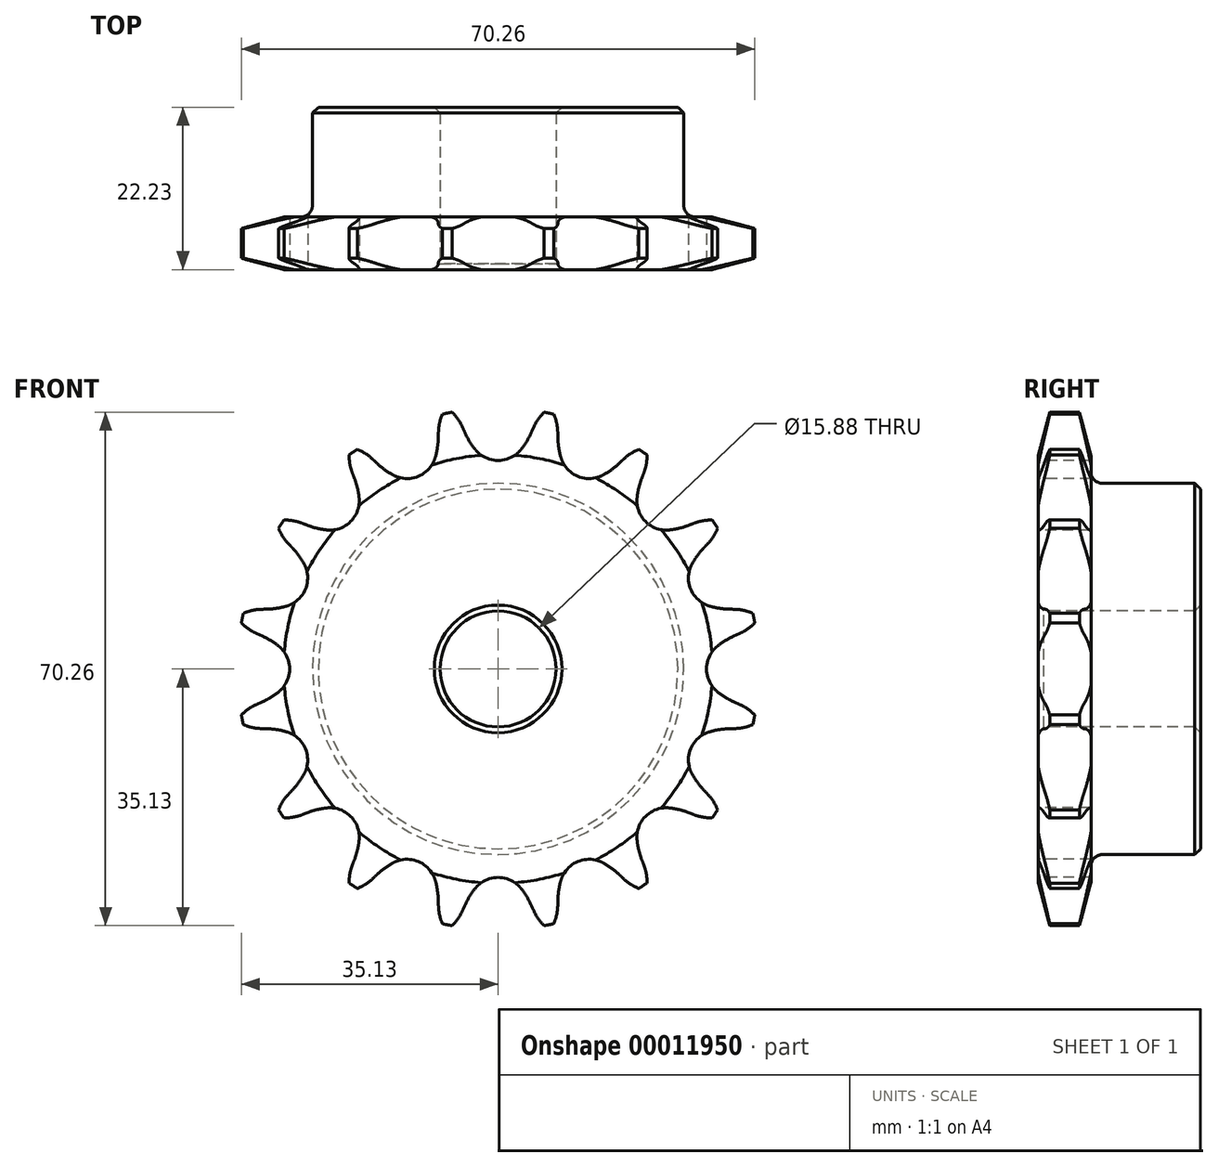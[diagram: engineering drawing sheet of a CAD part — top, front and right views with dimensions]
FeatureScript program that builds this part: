
annotation { "Feature Type Name" : "Feature", "Feature Type Description" : "" }
export const myFeature = defineFeature(function(context is Context, id is Id, definition is map)
    precondition{}
    {
        {
            var Q0;
            Q0=qCreatedBy(makeId("Right.planeOp"),FACE);
            var sketch = newSketch(context, id + "F0", { "sketchPlane" : qUnion([Q0])});
            skLineSegment(sketch, "E0", {"start": v(0, 0) * mm, "end": v(22.22, 0) * mm, "construction": true});
            skLineSegment(sketch, "E1", {"start": v(0, 35.69) * mm, "end": v(7.21, 35.69) * mm});
            skLineSegment(sketch, "E2", {"start": v(7.21, 35.69) * mm, "end": v(7.21, 25.4) * mm});
            skLineSegment(sketch, "E3", {"start": v(7.21, 25.4) * mm, "end": v(22.23, 25.4) * mm});
            skLineSegment(sketch, "E4", {"start": v(22.22, 25.4) * mm, "end": v(22.22, 7.94) * mm});
            skLineSegment(sketch, "E5", {"start": v(22.23, 7.94) * mm, "end": v(0, 7.94) * mm});
            skLineSegment(sketch, "E6", {"start": v(0, 7.94) * mm, "end": v(0, 35.69) * mm});
            skLineSegment(sketch, "E7.0.MirrorCS", {"start": v(0, -35.69) * mm, "end": v(7.21, -35.69) * mm});
            skLineSegment(sketch, "E7.1.MirrorCS", {"start": v(7.21, -35.69) * mm, "end": v(7.21, -25.4) * mm});
            skLineSegment(sketch, "E7.2.MirrorCS", {"start": v(22.23, -7.94) * mm, "end": v(0, -7.94) * mm});
            skLineSegment(sketch, "E7.3.MirrorCS", {"start": v(22.23, -25.4) * mm, "end": v(22.23, -7.94) * mm});
            skLineSegment(sketch, "E7.4.MirrorCS", {"start": v(7.21, -25.4) * mm, "end": v(22.23, -25.4) * mm});
            skLineSegment(sketch, "E7.5.MirrorCS", {"start": v(0, -7.94) * mm, "end": v(0, -35.69) * mm});
            skSolve(sketch);
        }
        {
            var Q0;
            Q0=makeQuery(id+"F0.imprint","IMPRINT",FACE,{"disambiguationData":[TD([[makeQuery(id+"F0.imprint","IMPRINT",EDGE,{"derivedFrom":sQuery(id+"F0.wireOp",EDGE,"E1")}),-1.0]])]});
            var Q1;
            Q1=sQuery(id+"F0.wireOp",EDGE,"E0");
            revolve(context, id + "F1", {"entities" : qUnion([Q0]), "axis" : qUnion([Q1]), "revolveType" : RevolveType.FULL});
        }
        {
            var Q0;
            Q0=makeQuery(id+"F1.opRevolve","SWEPT_EDGE",EDGE,{"disambiguationData":[OSD([sQuery(id+"F0.wireOp",EDGE,"E1"),sQuery(id+"F0.wireOp",EDGE,"E6")])]});
            var Q1;
            Q1=makeQuery(id+"F1.opRevolve","SWEPT_EDGE",EDGE,{"disambiguationData":[OSD([sQuery(id+"F0.wireOp",EDGE,"E1"),sQuery(id+"F0.wireOp",EDGE,"E2")])]});
            chamfer(context, id + "F2", {"entities" : qUnion([Q0, Q1]), "chamferType" : ChamferType.TWO_OFFSETS, "width1" : 6.35 * mm, "oppositeDirection" : false, "width2" : 1.57 * mm, "tangentPropagation" : true});
        }
        {
            var Q0;
            Q0=makeQuery(id+"F1.opRevolve","SWEPT_FACE",FACE,{"disambiguationData":[OSD([sQuery(id+"F0.wireOp",EDGE,"E6")])]});
            var sketch = newSketch(context, id + "F3", { "sketchPlane" : qUnion([Q0])});
            skCircle(sketch, "E8", {"center": v(0, 0) * mm, "radius": 32.55 * mm, "construction": true});
            skLineSegment(sketch, "E9", {"start": v(0, 0) * mm, "end": v(0, 32.55) * mm, "construction": true});
            skLineSegment(sketch, "E10", {"start": v(0, 32.55) * mm, "end": v(25.8, 32.55) * mm, "construction": true});
            skPoint(sketch, "E11", {"position": v(-10.88, 30.38) * mm});
            skPoint(sketch, "E12", {"position": v(4.95, 36.52) * mm});
            skLineSegment(sketch, "E13", {"start": v(0, 32.55) * mm, "end": v(4.95, 36.52) * mm, "construction": true});
            skLineSegment(sketch, "E14", {"start": v(4.95, 36.52) * mm, "end": v(-4.5, 32.26) * mm, "construction": true});
            skLineSegment(sketch, "E15", {"start": v(-4.5, 32.26) * mm, "end": v(-4.88, 33.1) * mm});
            skLineSegment(sketch, "E16", {"start": v(0, 0) * mm, "end": v(-7.12, 35.8) * mm, "construction": true});
            skArc(sketch, "E17", {"start": v(-7.12, 35.8) * mm, "mid": v(-15.95, 26.17) * mm, "end": v(-4.88, 33.1) * mm, "construction": true});
            skArc(sketch, "E18", {"start": v(-4.88, 33.1) * mm, "mid": v(-5.81, 34.6) * mm, "end": v(-7.12, 35.8) * mm});
            skArc(sketch, "E19", {"start": v(-3.14, 30.03) * mm, "mid": v(13.78, 41.93) * mm, "end": v(-4.5, 32.26) * mm, "construction": true});
            skArc(sketch, "E20", {"start": v(-4.5, 32.26) * mm, "mid": v(-3.89, 31.1) * mm, "end": v(-3.14, 30.03) * mm});
            skLineSegment(sketch, "E21", {"start": v(4.4, 12.5) * mm, "end": v(-4.88, 33.1) * mm, "construction": true});
            skArc(sketch, "E22.0.MirrorCS", {"start": v(4.5, 32.26) * mm, "mid": v(3.89, 31.1) * mm, "end": v(3.14, 30.03) * mm});
            skLineSegment(sketch, "E23.0.MirrorCS", {"start": v(4.5, 32.26) * mm, "end": v(4.88, 33.1) * mm});
            skArc(sketch, "E24.0.MirrorCS", {"start": v(4.88, 33.1) * mm, "mid": v(5.81, 34.6) * mm, "end": v(7.12, 35.8) * mm});
            skArc(sketch, "E25", {"start": v(-3.14, 30.03) * mm, "mid": v(0, 28.53) * mm, "end": v(3.14, 30.03) * mm});
            skArc(sketch, "E26", {"start": v(3.14, 30.03) * mm, "mid": v(0, 36.57) * mm, "end": v(-3.14, 30.03) * mm, "construction": true});
            skArc(sketch, "E27.1.0", {"start": v(-17.17, 28.7) * mm, "mid": v(-18.61, 29.74) * mm, "end": v(-20.28, 30.34) * mm});
            skLineSegment(sketch, "E27.1.1", {"start": v(-16.5, 28.08) * mm, "end": v(-17.17, 28.7) * mm});
            skArc(sketch, "E27.1.2", {"start": v(-16.5, 28.08) * mm, "mid": v(-15.5, 27.25) * mm, "end": v(-14.39, 26.55) * mm});
            skArc(sketch, "E27.1.3", {"start": v(-14.39, 26.55) * mm, "mid": v(-10.92, 26.36) * mm, "end": v(-8.6, 28.95) * mm});
            skArc(sketch, "E27.1.4", {"start": v(-8.19, 31.53) * mm, "mid": v(-8.3, 30.22) * mm, "end": v(-8.6, 28.95) * mm});
            skLineSegment(sketch, "E27.1.5", {"start": v(-8.19, 31.53) * mm, "end": v(-8.16, 32.44) * mm});
            skArc(sketch, "E27.1.6", {"start": v(-8.16, 32.44) * mm, "mid": v(-7.87, 34.19) * mm, "end": v(-7.12, 35.8) * mm});
            skArc(sketch, "E27.2.0", {"start": v(-26.85, 19.95) * mm, "mid": v(-28.57, 20.35) * mm, "end": v(-30.34, 20.28) * mm});
            skLineSegment(sketch, "E27.2.1", {"start": v(-26, 19.63) * mm, "end": v(-26.85, 19.95) * mm});
            skArc(sketch, "E27.2.2", {"start": v(-26, 19.63) * mm, "mid": v(-24.74, 19.24) * mm, "end": v(-23.45, 19.02) * mm});
            skArc(sketch, "E27.2.3", {"start": v(-23.45, 19.02) * mm, "mid": v(-20.17, 20.17) * mm, "end": v(-19.02, 23.45) * mm});
            skArc(sketch, "E27.2.4", {"start": v(-19.63, 26) * mm, "mid": v(-19.24, 24.74) * mm, "end": v(-19.02, 23.45) * mm});
            skLineSegment(sketch, "E27.2.5", {"start": v(-19.63, 26) * mm, "end": v(-19.95, 26.85) * mm});
            skArc(sketch, "E27.2.6", {"start": v(-19.95, 26.85) * mm, "mid": v(-20.35, 28.57) * mm, "end": v(-20.28, 30.34) * mm});
            skArc(sketch, "E27.3.0", {"start": v(-32.44, 8.16) * mm, "mid": v(-34.19, 7.87) * mm, "end": v(-35.8, 7.12) * mm});
            skLineSegment(sketch, "E27.3.1", {"start": v(-31.53, 8.19) * mm, "end": v(-32.44, 8.16) * mm});
            skArc(sketch, "E27.3.2", {"start": v(-31.53, 8.19) * mm, "mid": v(-30.22, 8.3) * mm, "end": v(-28.95, 8.6) * mm});
            skArc(sketch, "E27.3.3", {"start": v(-28.95, 8.6) * mm, "mid": v(-26.36, 10.92) * mm, "end": v(-26.55, 14.39) * mm});
            skArc(sketch, "E27.3.4", {"start": v(-28.08, 16.5) * mm, "mid": v(-27.25, 15.5) * mm, "end": v(-26.55, 14.39) * mm});
            skLineSegment(sketch, "E27.3.5", {"start": v(-28.08, 16.5) * mm, "end": v(-28.7, 17.17) * mm});
            skArc(sketch, "E27.3.6", {"start": v(-28.7, 17.17) * mm, "mid": v(-29.74, 18.61) * mm, "end": v(-30.34, 20.28) * mm});
            skArc(sketch, "E27.4.0", {"start": v(-33.1, -4.88) * mm, "mid": v(-34.6, -5.81) * mm, "end": v(-35.8, -7.12) * mm});
            skLineSegment(sketch, "E27.4.1", {"start": v(-32.26, -4.5) * mm, "end": v(-33.1, -4.88) * mm});
            skArc(sketch, "E27.4.2", {"start": v(-32.26, -4.5) * mm, "mid": v(-31.1, -3.89) * mm, "end": v(-30.03, -3.14) * mm});
            skArc(sketch, "E27.4.3", {"start": v(-30.03, -3.14) * mm, "mid": v(-28.53, 0) * mm, "end": v(-30.03, 3.14) * mm});
            skArc(sketch, "E27.4.4", {"start": v(-32.26, 4.5) * mm, "mid": v(-31.1, 3.89) * mm, "end": v(-30.03, 3.14) * mm});
            skLineSegment(sketch, "E27.4.5", {"start": v(-32.26, 4.5) * mm, "end": v(-33.1, 4.88) * mm});
            skArc(sketch, "E27.4.6", {"start": v(-33.1, 4.88) * mm, "mid": v(-34.6, 5.81) * mm, "end": v(-35.8, 7.12) * mm});
            skArc(sketch, "E27.5.0", {"start": v(-28.7, -17.17) * mm, "mid": v(-29.74, -18.61) * mm, "end": v(-30.34, -20.28) * mm});
            skLineSegment(sketch, "E27.5.1", {"start": v(-28.08, -16.5) * mm, "end": v(-28.7, -17.17) * mm});
            skArc(sketch, "E27.5.2", {"start": v(-28.08, -16.5) * mm, "mid": v(-27.25, -15.5) * mm, "end": v(-26.55, -14.39) * mm});
            skArc(sketch, "E27.5.3", {"start": v(-26.55, -14.39) * mm, "mid": v(-26.36, -10.92) * mm, "end": v(-28.95, -8.6) * mm});
            skArc(sketch, "E27.5.4", {"start": v(-31.53, -8.19) * mm, "mid": v(-30.22, -8.3) * mm, "end": v(-28.95, -8.6) * mm});
            skLineSegment(sketch, "E27.5.5", {"start": v(-31.53, -8.19) * mm, "end": v(-32.44, -8.16) * mm});
            skArc(sketch, "E27.5.6", {"start": v(-32.44, -8.16) * mm, "mid": v(-34.19, -7.87) * mm, "end": v(-35.8, -7.12) * mm});
            skArc(sketch, "E27.6.0", {"start": v(-19.95, -26.85) * mm, "mid": v(-20.35, -28.57) * mm, "end": v(-20.28, -30.34) * mm});
            skLineSegment(sketch, "E27.6.1", {"start": v(-19.63, -26) * mm, "end": v(-19.95, -26.85) * mm});
            skArc(sketch, "E27.6.2", {"start": v(-19.63, -26) * mm, "mid": v(-19.24, -24.74) * mm, "end": v(-19.02, -23.45) * mm});
            skArc(sketch, "E27.6.3", {"start": v(-19.02, -23.45) * mm, "mid": v(-20.17, -20.17) * mm, "end": v(-23.45, -19.02) * mm});
            skArc(sketch, "E27.6.4", {"start": v(-26, -19.63) * mm, "mid": v(-24.74, -19.24) * mm, "end": v(-23.45, -19.02) * mm});
            skLineSegment(sketch, "E27.6.5", {"start": v(-26, -19.63) * mm, "end": v(-26.85, -19.95) * mm});
            skArc(sketch, "E27.6.6", {"start": v(-26.85, -19.95) * mm, "mid": v(-28.57, -20.35) * mm, "end": v(-30.34, -20.28) * mm});
            skArc(sketch, "E27.7.0", {"start": v(-8.16, -32.44) * mm, "mid": v(-7.87, -34.19) * mm, "end": v(-7.12, -35.8) * mm});
            skLineSegment(sketch, "E27.7.1", {"start": v(-8.19, -31.53) * mm, "end": v(-8.16, -32.44) * mm});
            skArc(sketch, "E27.7.2", {"start": v(-8.19, -31.53) * mm, "mid": v(-8.3, -30.22) * mm, "end": v(-8.6, -28.95) * mm});
            skArc(sketch, "E27.7.3", {"start": v(-8.6, -28.95) * mm, "mid": v(-10.92, -26.36) * mm, "end": v(-14.39, -26.55) * mm});
            skArc(sketch, "E27.7.4", {"start": v(-16.5, -28.08) * mm, "mid": v(-15.5, -27.25) * mm, "end": v(-14.39, -26.55) * mm});
            skLineSegment(sketch, "E27.7.5", {"start": v(-16.5, -28.08) * mm, "end": v(-17.17, -28.7) * mm});
            skArc(sketch, "E27.7.6", {"start": v(-17.17, -28.7) * mm, "mid": v(-18.61, -29.74) * mm, "end": v(-20.28, -30.34) * mm});
            skArc(sketch, "E27.8.0", {"start": v(4.88, -33.1) * mm, "mid": v(5.81, -34.6) * mm, "end": v(7.12, -35.8) * mm});
            skLineSegment(sketch, "E27.8.1", {"start": v(4.5, -32.26) * mm, "end": v(4.88, -33.1) * mm});
            skArc(sketch, "E27.8.2", {"start": v(4.5, -32.26) * mm, "mid": v(3.89, -31.1) * mm, "end": v(3.14, -30.03) * mm});
            skArc(sketch, "E27.8.3", {"start": v(3.14, -30.03) * mm, "mid": v(0, -28.53) * mm, "end": v(-3.14, -30.03) * mm});
            skArc(sketch, "E27.8.4", {"start": v(-4.5, -32.26) * mm, "mid": v(-3.89, -31.1) * mm, "end": v(-3.14, -30.03) * mm});
            skLineSegment(sketch, "E27.8.5", {"start": v(-4.5, -32.26) * mm, "end": v(-4.88, -33.1) * mm});
            skArc(sketch, "E27.8.6", {"start": v(-4.88, -33.1) * mm, "mid": v(-5.81, -34.6) * mm, "end": v(-7.12, -35.8) * mm});
            skArc(sketch, "E27.9.0", {"start": v(17.17, -28.7) * mm, "mid": v(18.61, -29.74) * mm, "end": v(20.28, -30.34) * mm});
            skLineSegment(sketch, "E27.9.1", {"start": v(16.5, -28.08) * mm, "end": v(17.17, -28.7) * mm});
            skArc(sketch, "E27.9.2", {"start": v(16.5, -28.08) * mm, "mid": v(15.5, -27.25) * mm, "end": v(14.39, -26.55) * mm});
            skArc(sketch, "E27.9.3", {"start": v(14.39, -26.55) * mm, "mid": v(10.92, -26.36) * mm, "end": v(8.6, -28.95) * mm});
            skArc(sketch, "E27.9.4", {"start": v(8.19, -31.53) * mm, "mid": v(8.3, -30.22) * mm, "end": v(8.6, -28.95) * mm});
            skLineSegment(sketch, "E27.9.5", {"start": v(8.19, -31.53) * mm, "end": v(8.16, -32.44) * mm});
            skArc(sketch, "E27.9.6", {"start": v(8.16, -32.44) * mm, "mid": v(7.87, -34.19) * mm, "end": v(7.12, -35.8) * mm});
            skArc(sketch, "E27.10.0", {"start": v(26.85, -19.95) * mm, "mid": v(28.57, -20.35) * mm, "end": v(30.34, -20.28) * mm});
            skLineSegment(sketch, "E27.10.1", {"start": v(26, -19.63) * mm, "end": v(26.85, -19.95) * mm});
            skArc(sketch, "E27.10.2", {"start": v(26, -19.63) * mm, "mid": v(24.74, -19.24) * mm, "end": v(23.45, -19.02) * mm});
            skArc(sketch, "E27.10.3", {"start": v(23.45, -19.02) * mm, "mid": v(20.17, -20.17) * mm, "end": v(19.02, -23.45) * mm});
            skArc(sketch, "E27.10.4", {"start": v(19.63, -26) * mm, "mid": v(19.24, -24.74) * mm, "end": v(19.02, -23.45) * mm});
            skLineSegment(sketch, "E27.10.5", {"start": v(19.63, -26) * mm, "end": v(19.95, -26.85) * mm});
            skArc(sketch, "E27.10.6", {"start": v(19.95, -26.85) * mm, "mid": v(20.35, -28.57) * mm, "end": v(20.28, -30.34) * mm});
            skArc(sketch, "E27.11.0", {"start": v(32.44, -8.16) * mm, "mid": v(34.19, -7.87) * mm, "end": v(35.8, -7.12) * mm});
            skLineSegment(sketch, "E27.11.1", {"start": v(31.53, -8.19) * mm, "end": v(32.44, -8.16) * mm});
            skArc(sketch, "E27.11.2", {"start": v(31.53, -8.19) * mm, "mid": v(30.22, -8.3) * mm, "end": v(28.95, -8.6) * mm});
            skArc(sketch, "E27.11.3", {"start": v(28.95, -8.6) * mm, "mid": v(26.36, -10.92) * mm, "end": v(26.55, -14.39) * mm});
            skArc(sketch, "E27.11.4", {"start": v(28.08, -16.5) * mm, "mid": v(27.25, -15.5) * mm, "end": v(26.55, -14.39) * mm});
            skLineSegment(sketch, "E27.11.5", {"start": v(28.08, -16.5) * mm, "end": v(28.7, -17.17) * mm});
            skArc(sketch, "E27.11.6", {"start": v(28.7, -17.17) * mm, "mid": v(29.74, -18.61) * mm, "end": v(30.34, -20.28) * mm});
            skArc(sketch, "E27.12.0", {"start": v(33.1, 4.88) * mm, "mid": v(34.6, 5.81) * mm, "end": v(35.8, 7.12) * mm});
            skLineSegment(sketch, "E27.12.1", {"start": v(32.26, 4.5) * mm, "end": v(33.1, 4.88) * mm});
            skArc(sketch, "E27.12.2", {"start": v(32.26, 4.5) * mm, "mid": v(31.1, 3.89) * mm, "end": v(30.03, 3.14) * mm});
            skArc(sketch, "E27.12.3", {"start": v(30.03, 3.14) * mm, "mid": v(28.53, 0) * mm, "end": v(30.03, -3.14) * mm});
            skArc(sketch, "E27.12.4", {"start": v(32.26, -4.5) * mm, "mid": v(31.1, -3.89) * mm, "end": v(30.03, -3.14) * mm});
            skLineSegment(sketch, "E27.12.5", {"start": v(32.26, -4.5) * mm, "end": v(33.1, -4.88) * mm});
            skArc(sketch, "E27.12.6", {"start": v(33.1, -4.88) * mm, "mid": v(34.6, -5.81) * mm, "end": v(35.8, -7.12) * mm});
            skArc(sketch, "E27.13.0", {"start": v(28.7, 17.17) * mm, "mid": v(29.74, 18.61) * mm, "end": v(30.34, 20.28) * mm});
            skLineSegment(sketch, "E27.13.1", {"start": v(28.08, 16.5) * mm, "end": v(28.7, 17.17) * mm});
            skArc(sketch, "E27.13.2", {"start": v(28.08, 16.5) * mm, "mid": v(27.25, 15.5) * mm, "end": v(26.55, 14.39) * mm});
            skArc(sketch, "E27.13.3", {"start": v(26.55, 14.39) * mm, "mid": v(26.36, 10.92) * mm, "end": v(28.95, 8.6) * mm});
            skArc(sketch, "E27.13.4", {"start": v(31.53, 8.19) * mm, "mid": v(30.22, 8.3) * mm, "end": v(28.95, 8.6) * mm});
            skLineSegment(sketch, "E27.13.5", {"start": v(31.53, 8.19) * mm, "end": v(32.44, 8.16) * mm});
            skArc(sketch, "E27.13.6", {"start": v(32.44, 8.16) * mm, "mid": v(34.19, 7.87) * mm, "end": v(35.8, 7.12) * mm});
            skArc(sketch, "E27.14.0", {"start": v(19.95, 26.85) * mm, "mid": v(20.35, 28.57) * mm, "end": v(20.28, 30.34) * mm});
            skLineSegment(sketch, "E27.14.1", {"start": v(19.63, 26) * mm, "end": v(19.95, 26.85) * mm});
            skArc(sketch, "E27.14.2", {"start": v(19.63, 26) * mm, "mid": v(19.24, 24.74) * mm, "end": v(19.02, 23.45) * mm});
            skArc(sketch, "E27.14.3", {"start": v(19.02, 23.45) * mm, "mid": v(20.17, 20.17) * mm, "end": v(23.45, 19.02) * mm});
            skArc(sketch, "E27.14.4", {"start": v(26, 19.63) * mm, "mid": v(24.74, 19.24) * mm, "end": v(23.45, 19.02) * mm});
            skLineSegment(sketch, "E27.14.5", {"start": v(26, 19.63) * mm, "end": v(26.85, 19.95) * mm});
            skArc(sketch, "E27.14.6", {"start": v(26.85, 19.95) * mm, "mid": v(28.57, 20.35) * mm, "end": v(30.34, 20.28) * mm});
            skArc(sketch, "E27.15.0", {"start": v(8.16, 32.44) * mm, "mid": v(7.87, 34.19) * mm, "end": v(7.12, 35.8) * mm});
            skLineSegment(sketch, "E27.15.1", {"start": v(8.19, 31.53) * mm, "end": v(8.16, 32.44) * mm});
            skArc(sketch, "E27.15.2", {"start": v(8.19, 31.53) * mm, "mid": v(8.3, 30.22) * mm, "end": v(8.6, 28.95) * mm});
            skArc(sketch, "E27.15.3", {"start": v(8.6, 28.95) * mm, "mid": v(10.92, 26.36) * mm, "end": v(14.39, 26.55) * mm});
            skArc(sketch, "E27.15.4", {"start": v(16.5, 28.08) * mm, "mid": v(15.5, 27.25) * mm, "end": v(14.39, 26.55) * mm});
            skLineSegment(sketch, "E27.15.5", {"start": v(16.5, 28.08) * mm, "end": v(17.17, 28.7) * mm});
            skArc(sketch, "E27.15.6", {"start": v(17.17, 28.7) * mm, "mid": v(18.61, 29.74) * mm, "end": v(20.28, 30.34) * mm});
            skSolve(sketch);
        }
        {
            var Q0;
            Q0=qSketchRegion(id+"F3",true);
            extrude(context, id + "F4", {"entities" : qUnion([Q0]), "operationType" : NewBodyOperationType.INTERSECT, "endBound" : BoundingType.THROUGH_ALL, "oppositeDirection" : true, "depth" : 25.4 * mm});
        }
        {
            var Q0;
            Q0=makeQuery(id+"F1.opRevolve","SWEPT_EDGE",EDGE,{"disambiguationData":[OSD([sQuery(id+"F0.wireOp",EDGE,"E2"),sQuery(id+"F0.wireOp",EDGE,"E3")])]});
            fillet(context, id + "F5", {"entities" : qUnion([Q0]), "radius" : 1.59 * mm, "tangentPropagation" : true, "allowEdgeOverflow" : false});
        }
        {
            var Q0;
            Q0=makeQuery(id+"F1.opRevolve","SWEPT_EDGE",EDGE,{"disambiguationData":[OSD([sQuery(id+"F0.wireOp",EDGE,"E3"),sQuery(id+"F0.wireOp",EDGE,"E4")])]});
            var Q1;
            Q1=makeQuery(id+"F1.opRevolve","SWEPT_FACE",FACE,{"disambiguationData":[OSD([sQuery(id+"F0.wireOp",EDGE,"E5")])]});
            chamfer(context, id + "F6", {"entities" : qUnion([Q0, Q1]), "width" : 0.8 * mm, "tangentPropagation" : true});
        }
    });
